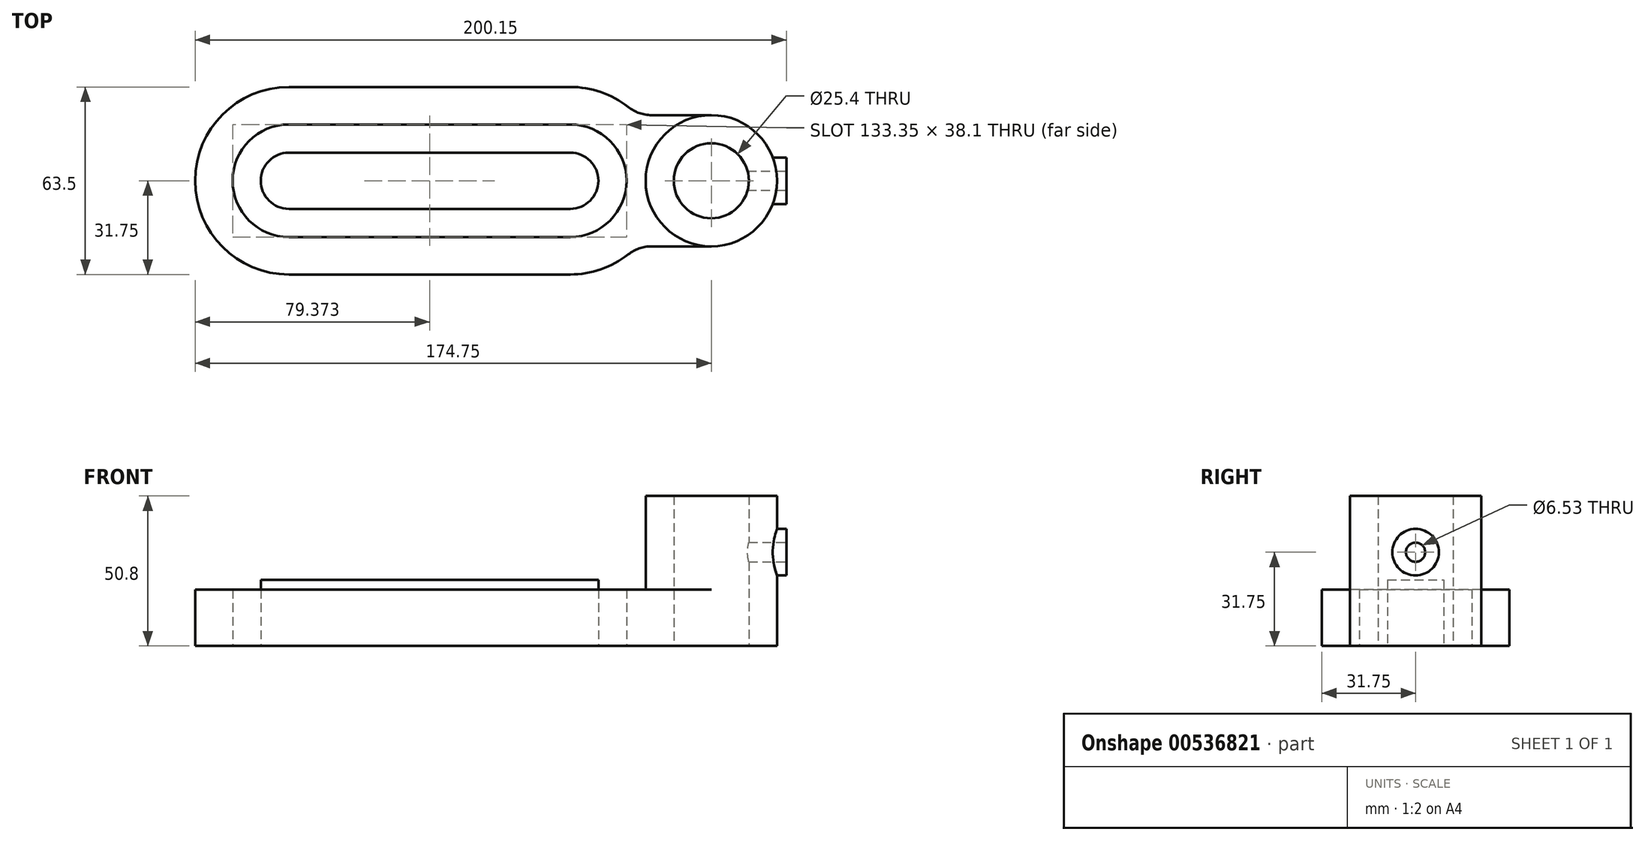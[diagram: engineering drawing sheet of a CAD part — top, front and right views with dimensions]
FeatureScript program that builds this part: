
annotation { "Feature Type Name" : "Feature", "Feature Type Description" : "" }
export const myFeature = defineFeature(function(context is Context, id is Id, definition is map)
    precondition{}
    {
        {
            var Q0;
            Q0=qCreatedBy(makeId("Top.planeOp"),FACE);
            var sketch = newSketch(context, id + "F0", { "sketchPlane" : qUnion([Q0])});
            skCircle(sketch, "E0", {"center": v(0, 0) * mm, "radius": 12.7 * mm});
            skCircle(sketch, "E1", {"center": v(0, 0) * mm, "radius": 22.23 * mm});
            skLineSegment(sketch, "E2", {"start": v(-47.75, 0) * mm, "end": v(-143, 0) * mm, "construction": true});
            skLineSegment(sketch, "E3", {"start": v(-143, 0) * mm, "end": v(-143, 0) * mm});
            skArc(sketch, "E4.0.startCap", {"start": v(-47.75, 9.53) * mm, "mid": v(-38.23, 0) * mm, "end": v(-47.75, -9.52) * mm});
            skArc(sketch, "E4.0.endCap", {"start": v(-143, -9.53) * mm, "mid": v(-152.53, 0) * mm, "end": v(-143, 9.52) * mm});
            skLineSegment(sketch, "E4.0.left", {"start": v(-47.75, -9.52) * mm, "end": v(-143, -9.53) * mm});
            skLineSegment(sketch, "E4.0.right", {"start": v(-47.75, 9.53) * mm, "end": v(-143, 9.52) * mm});
            skArc(sketch, "E5.0.startCap", {"start": v(-47.75, 19.05) * mm, "mid": v(-28.7, 0) * mm, "end": v(-47.75, -19.05) * mm});
            skArc(sketch, "E5.0.endCap", {"start": v(-143, -19.05) * mm, "mid": v(-162.05, 0) * mm, "end": v(-143, 19.05) * mm});
            skLineSegment(sketch, "E5.0.left", {"start": v(-47.75, -19.05) * mm, "end": v(-143, -19.05) * mm});
            skLineSegment(sketch, "E5.0.right", {"start": v(-47.75, 19.05) * mm, "end": v(-143, 19.05) * mm});
            skArc(sketch, "E6.0.startCap", {"start": v(-47.75, 31.75) * mm, "mid": v(-37.36, 30) * mm, "end": v(-28.11, 24.95) * mm});
            skArc(sketch, "E6.0.endCap", {"start": v(-143, -31.75) * mm, "mid": v(-174.75, 0) * mm, "end": v(-143, 31.75) * mm});
            skLineSegment(sketch, "E6.0.left", {"start": v(-47.75, -31.75) * mm, "end": v(-143, -31.75) * mm});
            skLineSegment(sketch, "E6.0.right", {"start": v(-47.75, 31.75) * mm, "end": v(-143, 31.75) * mm});
            skLineSegment(sketch, "E7", {"start": v(0, 22.23) * mm, "end": v(-20.26, 22.23) * mm});
            skArc(sketch, "E8.filletArc", {"start": v(-28.11, 24.95) * mm, "mid": v(-24.41, 22.92) * mm, "end": v(-20.26, 22.22) * mm});
            skArc(sketch, "E9.MirrorCS", {"start": v(-28.11, -24.95) * mm, "mid": v(-24.41, -22.92) * mm, "end": v(-20.26, -22.22) * mm});
            skArc(sketch, "E10.MirrorCS", {"start": v(-47.75, -31.75) * mm, "mid": v(-37.36, -30) * mm, "end": v(-28.11, -24.95) * mm});
            skLineSegment(sketch, "E11", {"start": v(-20.26, -22.22) * mm, "end": v(0, -22.22) * mm});
            skSolve(sketch);
        }
        {
            var Q0;
            Q0=makeQuery(id+"F0.imprint","IMPRINT",FACE,{"disambiguationData":[TD([[makeQuery(id+"F0.imprint","IMPRINT",EDGE,{"derivedFrom":sQuery(id+"F0.wireOp",EDGE,"E0")}),-1.0]])]});
            extrude(context, id + "F1", {"entities" : qUnion([Q0]), "depth" : 50.8 * mm, "offsetDistance" : 25.4 * mm});
        }
        {
            var Q0;
            Q0 = qSketchRegion(id + "F0", true);
            extrude(context, id + "F2", {"entities" : qUnion([Q0]), "operationType" : NewBodyOperationType.ADD, "depth" : 19.05 * mm, "offsetDistance" : 25.4 * mm});
        }
        {
            var Q0;
            Q0=makeQuery(id+"F0.imprint","IMPRINT",FACE,{"disambiguationData":[TD([[makeQuery(id+"F0.imprint","IMPRINT",EDGE,{"derivedFrom":sQuery(id+"F0.wireOp",EDGE,"E4.0.startCap")}),1.0]])]});
            extrude(context, id + "F3", {"entities" : qUnion([Q0]), "operationType" : NewBodyOperationType.ADD, "depth" : 22.35 * mm, "offsetDistance" : 25.4 * mm});
        }
        {
            var Q0;
            Q0=qCreatedBy(makeId("Right.planeOp"),FACE);
            cPlane(context, id + "F4", {"entities" : qUnion([Q0]), "cplaneType" : CPlaneType.OFFSET, "offset" : 25.4 * mm, "width" : 152.4 * mm, "height" : 152.4 * mm});
        }
        {
            var Q0;
            Q0=qCreatedBy(id+"F4.planeOp",FACE);
            var sketch = newSketch(context, id + "F5", { "sketchPlane" : qUnion([Q0])});
            skCircle(sketch, "E12", {"center": v(0, 31.75) * mm, "radius": 3.26 * mm});
            skCircle(sketch, "E13", {"center": v(0, 31.75) * mm, "radius": 7.87 * mm});
            skSolve(sketch);
        }
        {
            var Q0;
            Q0 = qSketchRegion(id + "F5", true);
            extrude(context, id + "F6", {"entities" : qUnion([Q0]), "operationType" : NewBodyOperationType.ADD, "endBound" : BoundingType.UP_TO_NEXT, "oppositeDirection" : true, "depth" : 25.4 * mm, "offsetDistance" : 25.4 * mm});
        }
        {
            var Q0;
            Q0=makeQuery(id+"F5.imprint","IMPRINT",FACE,{"disambiguationData":[TD([[makeQuery(id+"F5.imprint","IMPRINT",EDGE,{"derivedFrom":sQuery(id+"F5.wireOp",EDGE,"E12")}),1.0]])]});
            extrude(context, id + "F7", {"entities" : qUnion([Q0]), "operationType" : NewBodyOperationType.REMOVE, "oppositeDirection" : true, "depth" : 19.05 * mm, "offsetDistance" : 25.4 * mm});
        }
    });
